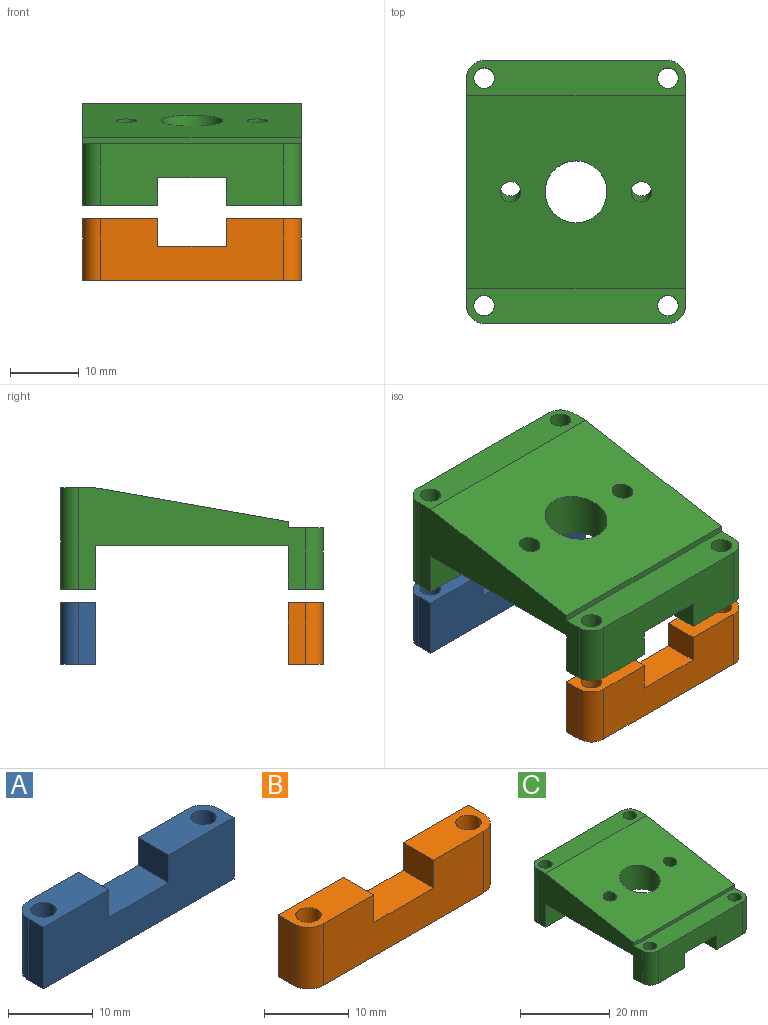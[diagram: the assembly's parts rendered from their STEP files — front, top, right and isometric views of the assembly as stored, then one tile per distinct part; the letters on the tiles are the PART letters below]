
ASSEMBLY  parts=3 mates=1
PART A: 14 faces, bbox 31.8x5.1x8.9 mm
  f0: plane 10.88x5.08mm, normal (0,0,1), area 46.8mm2, adj f1,f2,f3,f4,f6,f13
  f1: plane 31.75x8.89mm, normal (0,-1,0), area 242.3mm2, adj f0,f3,f8,f9,f10,f11,f12,f13
  f2: plane 26.67x8.89mm, normal (0,1,0), area 197.1mm2, adj f0,f4,f5,f9,f10,f11,f12,f13
  f3: plane 8.89x2.54mm, normal (1,0,0), area 22.6mm2, adj f0,f1,f4,f10
  f4: cylinder r=2.54mm len=8.89mm, axis (0,0,-1), area 35.5mm2, adj f0,f2,f3,f10
  f5: cylinder r=2.54mm len=8.89mm, axis (0,0,-1), area 35.5mm2, adj f2,f8,f9,f10
  f6: cylinder r=1.5mm len=8.89mm, axis (0,0,-1), area 83.8mm2, adj f0,f10
  f7: cylinder r=1.5mm len=8.89mm, axis (0,0,-1), area 83.8mm2, adj f9,f10
  f8: plane 8.89x2.54mm, normal (-1,0,0), area 22.6mm2, adj f1,f5,f9,f10
  f9: plane 10.88x5.08mm, normal (0,0,1), area 46.8mm2, adj f1,f2,f5,f7,f8,f11
  f10: plane 31.75x5.08mm, normal (0,0,-1), area 144.4mm2, adj f1,f2,f3,f4,f5,f6,f7,f8
  f11: plane 5.08x4mm, normal (1,0,0), area 20.3mm2, adj f1,f2,f9,f12
  f12: plane 10x5.08mm, normal (0,0,1), area 50.8mm2, adj f1,f2,f11,f13
  f13: plane 5.08x4mm, normal (-1,0,0), area 20.3mm2, adj f0,f1,f2,f12
PART B: 14 faces, bbox 31.8x5.1x8.9 mm
  f0: plane 10.88x5.08mm, normal (0,0,1), area 46.8mm2, adj f1,f2,f5,f6,f7,f13
  f1: plane 26.67x8.89mm, normal (0,-1,0), area 197.1mm2, adj f0,f4,f5,f9,f10,f11,f12,f13
  f2: plane 31.75x8.89mm, normal (0,1,0), area 242.3mm2, adj f0,f3,f6,f9,f10,f11,f12,f13
  f3: plane 8.89x2.54mm, normal (-1,0,0), area 22.6mm2, adj f2,f4,f9,f10
  f4: cylinder r=2.54mm len=8.89mm, axis (0,0,-1), area 35.5mm2, adj f1,f3,f9,f10
  f5: cylinder r=2.54mm len=8.89mm, axis (0,0,-1), area 35.5mm2, adj f0,f1,f6,f10
  f6: plane 8.89x2.54mm, normal (1,0,0), area 22.6mm2, adj f0,f2,f5,f10
  f7: cylinder r=1.5mm len=8.89mm, axis (0,0,-1), area 83.8mm2, adj f0,f10
  f8: cylinder r=1.5mm len=8.89mm, axis (0,0,-1), area 83.8mm2, adj f9,f10
  f9: plane 10.88x5.08mm, normal (0,0,1), area 46.8mm2, adj f1,f2,f3,f4,f8,f11
  f10: plane 31.75x5.08mm, normal (0,0,-1), area 144.4mm2, adj f1,f2,f3,f4,f5,f6,f7,f8
  f11: plane 5.08x4mm, normal (1,0,0), area 20.3mm2, adj f1,f2,f9,f12
  f12: plane 10x5.08mm, normal (0,0,1), area 50.8mm2, adj f1,f2,f11,f13
  f13: plane 5.08x4mm, normal (-1,0,0), area 20.3mm2, adj f0,f1,f2,f12
PART C: 36 faces, bbox 31.8x38.1x14.7 mm
  f0: cylinder r=1.5mm len=5.52mm, axis (0,-0.17,0.98), area 47.9mm2, adj f4,f35
  f1: cylinder r=1.5mm len=5.52mm, axis (0,-0.17,0.98), area 47.9mm2, adj f4,f33
  f2: plane 33.02x14.71mm, normal (1,0,0), area 224.8mm2, adj f4,f6,f15,f16,f17,f18,f19,f21
  f3: plane 33.02x14.71mm, normal (-1,0,0), area 224.8mm2, adj f4,f7,f8,f18,f19,f20,f21,f22
  f4: plane 31.75x27.91mm, normal (0,-0.17,0.98), area 821mm2, adj f0,f1,f2,f3,f10,f29,f31
  f5: plane 26.67x14.71mm, normal (0,1,0), area 352.2mm2, adj f6,f7,f17,f22,f23,f24,f25,f29
  f6: cylinder r=2.54mm len=14.71mm, axis (0,0,-1), area 58.7mm2, adj f2,f5,f17,f29
  f7: cylinder r=2.54mm len=14.71mm, axis (0,0,-1), area 58.7mm2, adj f3,f5,f22,f29
  f8: cylinder r=2.54mm len=8.89mm, axis (0,0,-1), area 35.5mm2, adj f3,f9,f20,f30
  f9: plane 26.67x8.89mm, normal (0,-1,0), area 197.1mm2, adj f8,f15,f16,f20,f26,f27,f28,f30
  f10: cylinder r=4.5mm len=9mm, axis (0,0,-1), area 166.8mm2, adj f4,f18
  f11: cylinder r=1.5mm len=14.71mm, axis (0,0,-1), area 138.6mm2, adj f22,f29
  f12: cylinder r=1.5mm len=14.71mm, axis (0,0,-1), area 138.6mm2, adj f17,f29
  f13: cylinder r=1.5mm len=8.89mm, axis (0,0,-1), area 83.8mm2, adj f20,f30
  f14: cylinder r=1.5mm len=8.89mm, axis (0,0,-1), area 83.8mm2, adj f16,f30
  f15: cylinder r=2.54mm len=8.89mm, axis (0,0,-1), area 35.5mm2, adj f2,f9,f16,f30
  f16: plane 10.88x5.08mm, normal (0,0,-1), area 46.8mm2, adj f2,f9,f14,f15,f19,f27
  f17: plane 10.88x5.08mm, normal (0,0,-1), area 46.8mm2, adj f2,f5,f6,f12,f21,f23
  f18: plane 31.75x27.94mm, normal (0,0,-1), area 766.1mm2, adj f2,f3,f10,f19,f21,f32,f34
  f19: plane 31.75x6.35mm, normal (0,1,0), area 161.6mm2, adj f2,f3,f16,f18,f20,f26,f27,f28
  f20: plane 10.88x5.08mm, normal (0,0,-1), area 46.8mm2, adj f3,f8,f9,f13,f19,f28
  f21: plane 31.75x6.35mm, normal (0,-1,0), area 161.6mm2, adj f2,f3,f17,f18,f22,f23,f24,f25
  f22: plane 10.88x5.08mm, normal (0,0,-1), area 46.8mm2, adj f3,f5,f7,f11,f21,f24
  f23: plane 5.08x4mm, normal (-1,0,0), area 20.3mm2, adj f5,f17,f21,f25
  f24: plane 5.08x4mm, normal (1,0,0), area 20.3mm2, adj f5,f21,f22,f25
  f25: plane 10x5.08mm, normal (0,0,-1), area 50.8mm2, adj f5,f21,f23,f24
  f26: plane 10x5.08mm, normal (0,0,-1), area 50.8mm2, adj f9,f19,f27,f28
  f27: plane 5.08x4mm, normal (-1,0,0), area 20.3mm2, adj f9,f16,f19,f26
  f28: plane 5.08x4mm, normal (1,0,0), area 20.3mm2, adj f9,f19,f20,f26
  f29: plane 31.75x5.11mm, normal (0,0,1), area 145.4mm2, adj f2,f3,f4,f5,f6,f7,f11,f12
  f30: plane 31.75x5.08mm, normal (0,0,1), area 144.4mm2, adj f2,f3,f8,f9,f13,f14,f15,f31
  f31: plane 31.75x0.9mm, normal (0,-1,0), area 28.4mm2, adj f2,f3,f4,f30
  f32: cylinder r=3mm len=6.16mm, axis (0,-0.17,0.98), area 17.2mm2, adj f18,f33
  f33: plane 6x5.91mm, normal (0,0.17,-0.98), area 21.2mm2, adj f1,f32
  f34: cylinder r=3mm len=6.16mm, axis (0,-0.17,0.98), area 17.2mm2, adj f18,f35
  f35: plane 6x5.91mm, normal (0,0.17,-0.98), area 21.2mm2, adj f0,f34
PLACE A t=(-6.61,15.3,15.51)mm
PLACE B t=(-6.61,15.3,15.51)mm
PLACE C t=(-6.61,17.03,32.75)mm
MATE fastened B.f5 <-> C.f14  axis (0,0,1) through (6.72,0.52,24.4)mm
